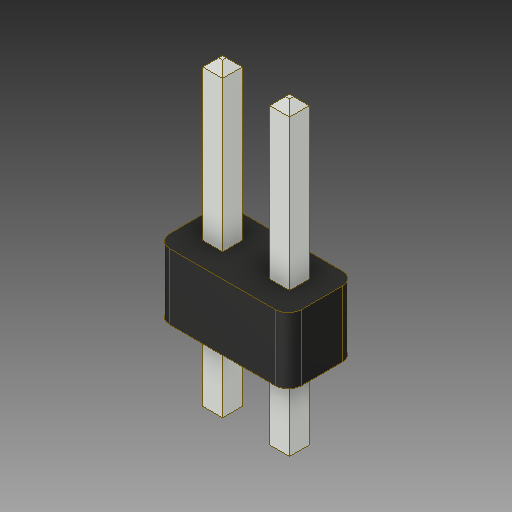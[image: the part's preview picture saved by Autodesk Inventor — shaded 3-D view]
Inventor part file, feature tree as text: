
AUTODESK INVENTOR PART (.ipt)
format: ipt  version: 2019 (Build 230136000, 136)  size: 115,712 bytes
history: native  units: in
note: dims shown in document units (in); Inventor stores cm internally (conversion verified against a paired STEP export)
features: chamfer x1
ambient origin geometry x8: Origin, YZ Plane, XZ Plane, XY Plane, X Axis, Y Axis, Z Axis, Center Point
bodies: Solid1 (feature_tree)
feature tree (1):
  chamfer  "Chamfer1"  [1 undecoded]
note: 1 required parameter value undecoded (feature->parameter linkage not recoverable at this tier; creation-order binding heuristic only, values carry confidence <= 0.55)
